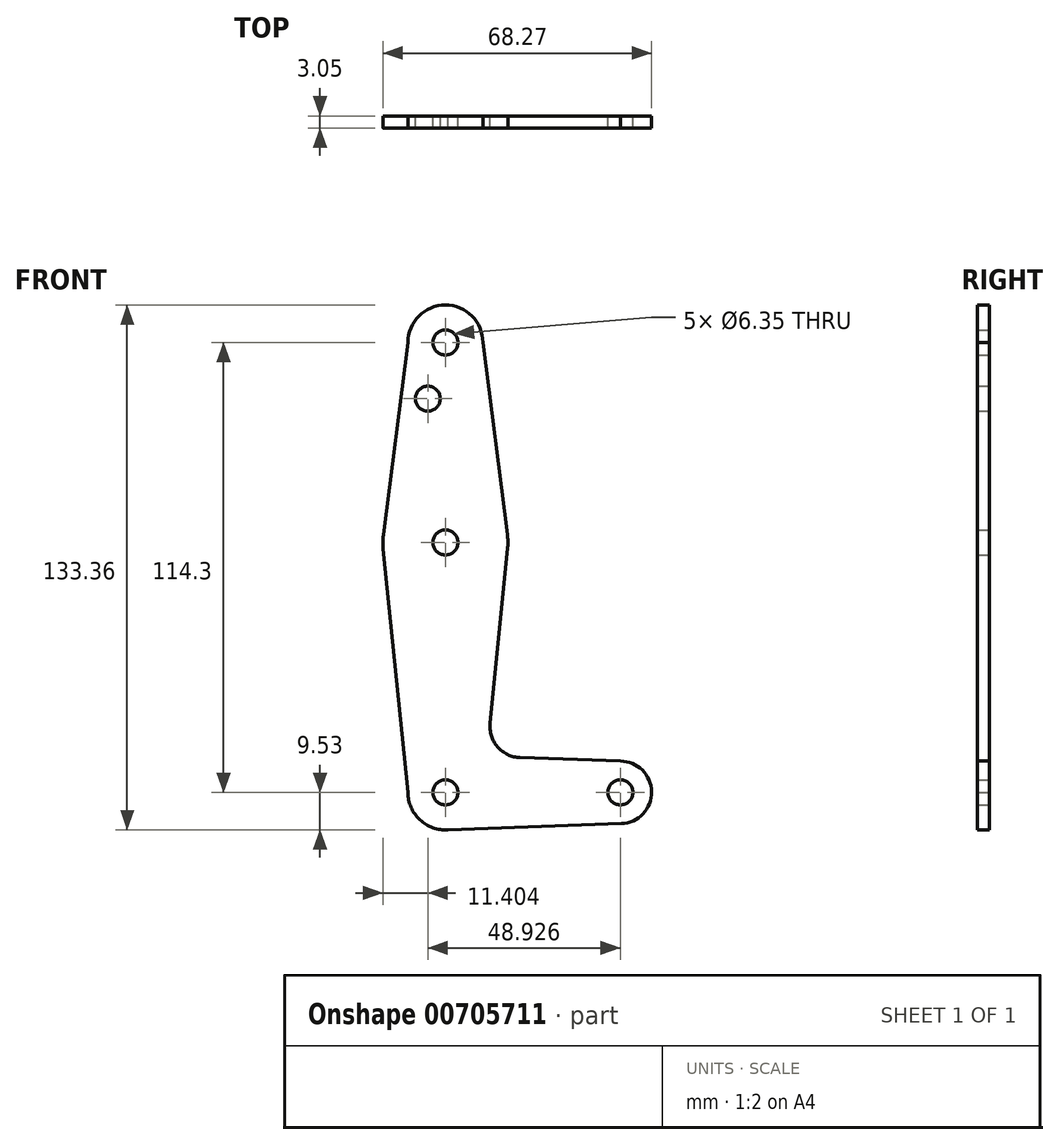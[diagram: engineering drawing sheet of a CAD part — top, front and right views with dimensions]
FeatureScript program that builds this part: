
annotation { "Feature Type Name" : "Feature", "Feature Type Description" : "" }
export const myFeature = defineFeature(function(context is Context, id is Id, definition is map)
    precondition{}
    {
        {
            var Q0;
            Q0=qCreatedBy(makeId("Front.planeOp"),FACE);
            var sketch = newSketch(context, id + "F0", { "sketchPlane" : qUnion([Q0])});
            skLineSegment(sketch, "E0", {"start": v(44.45, 0) * mm, "end": v(0, 0) * mm});
            skLineSegment(sketch, "E1", {"start": v(0, 0) * mm, "end": v(0, 63.5) * mm});
            skLineSegment(sketch, "E2", {"start": v(0, 114.3) * mm, "end": v(0, 63.5) * mm});
            skCircle(sketch, "E3", {"center": v(0, 0) * mm, "radius": 9.53 * mm});
            skCircle(sketch, "E4", {"center": v(44.45, 0) * mm, "radius": 7.94 * mm});
            skCircle(sketch, "E5", {"center": v(0, 114.3) * mm, "radius": 9.53 * mm});
            skCircle(sketch, "E6", {"center": v(0, 63.5) * mm, "radius": 15.88 * mm});
            skLineSegment(sketch, "E7.left", {"start": v(0, 0) * mm, "end": v(0, 0) * mm});
            skCircle(sketch, "E8", {"center": v(0, 114.3) * mm, "radius": 3.18 * mm});
            skCircle(sketch, "E9", {"center": v(0, 63.5) * mm, "radius": 3.18 * mm});
            skCircle(sketch, "E10", {"center": v(0, 0) * mm, "radius": 3.18 * mm});
            skCircle(sketch, "E11", {"center": v(44.45, 0) * mm, "radius": 3.18 * mm});
            skLineSegment(sketch, "E12", {"start": v(9.52, 114.3) * mm, "end": v(15.75, 65.5) * mm});
            skLineSegment(sketch, "E13", {"start": v(-9.52, 114.3) * mm, "end": v(-15.75, 65.5) * mm});
            skLineSegment(sketch, "E14", {"start": v(15.8, 61.91) * mm, "end": v(11.34, 17.59) * mm});
            skLineSegment(sketch, "E15", {"start": v(-9.52, 0) * mm, "end": v(-15.8, 61.9) * mm});
            skLineSegment(sketch, "E16", {"start": v(0, -9.53) * mm, "end": v(44.73, -7.93) * mm});
            skLineSegment(sketch, "E17", {"start": v(44.45, 7.94) * mm, "end": v(18.97, 8.85) * mm});
            skArc(sketch, "E18.filletArc", {"start": v(11.34, 17.59) * mm, "mid": v(13.26, 11.57) * mm, "end": v(18.97, 8.85) * mm});
            skCircle(sketch, "E19", {"center": v(-4.48, 100.03) * mm, "radius": 3.18 * mm});
            skSolve(sketch);
        }
        {
            var Q0;
            Q0 = qSketchRegion(id + "F0", true);
            var Q1;
            {var subQ0=sQuery(id+"F0.wireOp",EDGE,"E3");var subQ1=sQuery(id+"F0.wireOp",EDGE,"E0");var subQ2=makeQuery(id+"F0.imprint","INTERSECT",VERTEX,{"derivedFrom":[subQ1,subQ0]});Q1=makeQuery(id+"F0.imprint","IMPRINT",FACE,{"disambiguationData":[TD([[makeQuery(id+"F0.imprint","IMPRINT",EDGE,{"disambiguationData":[TD([[subQ2,-1.0]])],"derivedFrom":subQ1}),-1.0]])]});}
            extrude(context, id + "F1", {"entities" : qUnion([Q0, Q1]), "depth" : 3.05 * mm, "offsetDistance" : 25.4 * mm});
        }
    });
